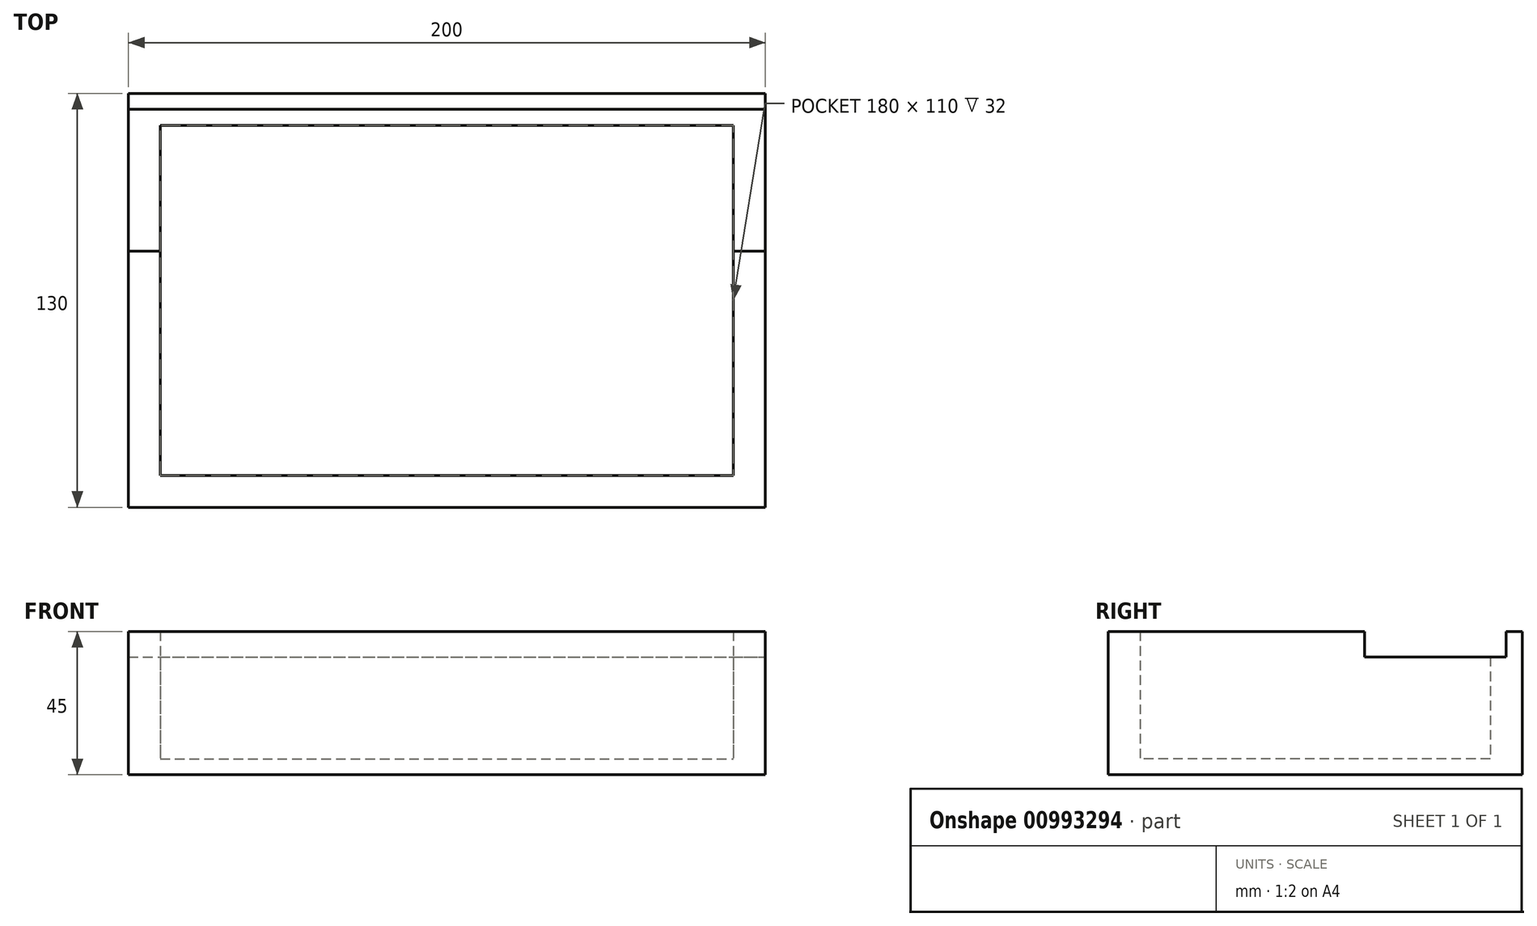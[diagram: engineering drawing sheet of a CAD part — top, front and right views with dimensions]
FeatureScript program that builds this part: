
annotation { "Feature Type Name" : "Feature", "Feature Type Description" : "" }
export const myFeature = defineFeature(function(context is Context, id is Id, definition is map)
    precondition{}
    {
        {
            var Q0;
            Q0=qCreatedBy(makeId("Top.planeOp"),FACE);
            var sketch = newSketch(context, id + "F0", { "sketchPlane" : qUnion([Q0])});
            skLineSegment(sketch, "E0.bottom", {"start": v(100, 65) * mm, "end": v(-100, 65) * mm});
            skLineSegment(sketch, "E0.top", {"start": v(100, -65) * mm, "end": v(-100, -65) * mm});
            skLineSegment(sketch, "E0.left", {"start": v(100, 65) * mm, "end": v(100, -65) * mm});
            skLineSegment(sketch, "E0.right", {"start": v(-100, 65) * mm, "end": v(-100, -65) * mm});
            skPoint(sketch, "E0.middle", {"position": v(0, 0) * mm});
            skSolve(sketch);
        }
        {
            var Q0;
            Q0 = qSketchRegion(id + "F0", true);
            extrude(context, id + "F1", {"entities" : qUnion([Q0]), "depth" : 5 * mm, "offsetDistance" : 25 * mm});
        }
        {
            var Q0;
            Q0=makeQuery(id+"F1.opExtrude","CAP_FACE",FACE,{"disambiguationData":[OSD([sQuery(id+"F0.wireOp",EDGE,"E0.bottom"),sQuery(id+"F0.wireOp",EDGE,"E0.top"),sQuery(id+"F0.wireOp",EDGE,"E0.left"),sQuery(id+"F0.wireOp",EDGE,"E0.right")])],"isStart":false});
            var sketch = newSketch(context, id + "F2", { "sketchPlane" : qUnion([Q0])});
            skLineSegment(sketch, "E1.bottom", {"start": v(-100, 65) * mm, "end": v(100, 65) * mm});
            skLineSegment(sketch, "E1.top", {"start": v(-100, 55) * mm, "end": v(100, 55) * mm});
            skLineSegment(sketch, "E1.left", {"start": v(-100, 65) * mm, "end": v(-100, 55) * mm});
            skLineSegment(sketch, "E1.right", {"start": v(100, 65) * mm, "end": v(100, 55) * mm});
            skSolve(sketch);
        }
        {
            var Q0;
            Q0 = qSketchRegion(id + "F2", true);
            extrude(context, id + "F3", {"entities" : qUnion([Q0]), "operationType" : NewBodyOperationType.ADD, "depth" : 32 * mm, "offsetDistance" : 25 * mm});
        }
        {
            var Q0;
            Q0=makeQuery(id+"F3.opExtrude","CAP_FACE",FACE,{"disambiguationData":[OSD([sQuery(id+"F2.wireOp",EDGE,"E1.bottom"),sQuery(id+"F2.wireOp",EDGE,"E1.top"),sQuery(id+"F2.wireOp",EDGE,"E1.left"),sQuery(id+"F2.wireOp",EDGE,"E1.right")])],"isStart":false});
            var sketch = newSketch(context, id + "F4", { "sketchPlane" : qUnion([Q0])});
            skLineSegment(sketch, "E2.bottom", {"start": v(-100, 65) * mm, "end": v(100, 65) * mm});
            skLineSegment(sketch, "E2.top", {"start": v(-100, 60) * mm, "end": v(100, 60) * mm});
            skLineSegment(sketch, "E2.left", {"start": v(-100, 65) * mm, "end": v(-100, 60) * mm});
            skLineSegment(sketch, "E2.right", {"start": v(100, 65) * mm, "end": v(100, 60) * mm});
            skSolve(sketch);
        }
        {
            var Q0;
            Q0 = qSketchRegion(id + "F4", true);
            extrude(context, id + "F5", {"entities" : qUnion([Q0]), "operationType" : NewBodyOperationType.ADD, "depth" : 8 * mm, "offsetDistance" : 25 * mm});
        }
        {
            var Q0;
            Q0=makeQuery(id+"F1.opExtrude","CAP_FACE",FACE,{"disambiguationData":[OSD([sQuery(id+"F0.wireOp",EDGE,"E0.bottom"),sQuery(id+"F0.wireOp",EDGE,"E0.top"),sQuery(id+"F0.wireOp",EDGE,"E0.left"),sQuery(id+"F0.wireOp",EDGE,"E0.right")])],"isStart":false});
            var sketch = newSketch(context, id + "F6", { "sketchPlane" : qUnion([Q0])});
            skLineSegment(sketch, "E3.bottom", {"start": v(-100, 55) * mm, "end": v(-90, 55) * mm});
            skLineSegment(sketch, "E3.top", {"start": v(-100, -65) * mm, "end": v(-90, -65) * mm});
            skLineSegment(sketch, "E3.left", {"start": v(-100, 55) * mm, "end": v(-100, -65) * mm});
            skLineSegment(sketch, "E3.right", {"start": v(-90, 55) * mm, "end": v(-90, -65) * mm});
            skSolve(sketch);
        }
        {
            var Q0;
            Q0 = qSketchRegion(id + "F6", true);
            extrude(context, id + "F7", {"entities" : qUnion([Q0]), "operationType" : NewBodyOperationType.ADD, "depth" : 32 * mm, "offsetDistance" : 25 * mm});
        }
        {
            var Q0;
            Q0=makeQuery(id+"F1.opExtrude","CAP_FACE",FACE,{"disambiguationData":[OSD([sQuery(id+"F0.wireOp",EDGE,"E0.bottom"),sQuery(id+"F0.wireOp",EDGE,"E0.top"),sQuery(id+"F0.wireOp",EDGE,"E0.left"),sQuery(id+"F0.wireOp",EDGE,"E0.right")])],"isStart":false});
            var sketch = newSketch(context, id + "F8", { "sketchPlane" : qUnion([Q0])});
            skLineSegment(sketch, "E4.bottom", {"start": v(100, 55) * mm, "end": v(90, 55) * mm});
            skLineSegment(sketch, "E4.top", {"start": v(100, -65) * mm, "end": v(90, -65) * mm});
            skLineSegment(sketch, "E4.left", {"start": v(100, 55) * mm, "end": v(100, -65) * mm});
            skLineSegment(sketch, "E4.right", {"start": v(90, 55) * mm, "end": v(90, -65) * mm});
            skSolve(sketch);
        }
        {
            var Q0;
            Q0 = qSketchRegion(id + "F8", true);
            extrude(context, id + "F9", {"entities" : qUnion([Q0]), "operationType" : NewBodyOperationType.ADD, "depth" : 32 * mm, "offsetDistance" : 25 * mm});
        }
        {
            var Q0;
            Q0=makeQuery(id+"F1.opExtrude","CAP_FACE",FACE,{"disambiguationData":[OSD([sQuery(id+"F0.wireOp",EDGE,"E0.bottom"),sQuery(id+"F0.wireOp",EDGE,"E0.top"),sQuery(id+"F0.wireOp",EDGE,"E0.left"),sQuery(id+"F0.wireOp",EDGE,"E0.right")])],"isStart":false});
            var sketch = newSketch(context, id + "F10", { "sketchPlane" : qUnion([Q0])});
            skLineSegment(sketch, "E5.bottom", {"start": v(-90, -65) * mm, "end": v(90, -65) * mm});
            skLineSegment(sketch, "E5.top", {"start": v(-90, -55) * mm, "end": v(90, -55) * mm});
            skLineSegment(sketch, "E5.left", {"start": v(-90, -65) * mm, "end": v(-90, -55) * mm});
            skLineSegment(sketch, "E5.right", {"start": v(90, -65) * mm, "end": v(90, -55) * mm});
            skSolve(sketch);
        }
        {
            var Q0;
            Q0 = qSketchRegion(id + "F10", true);
            extrude(context, id + "F11", {"entities" : qUnion([Q0]), "operationType" : NewBodyOperationType.ADD, "depth" : 40 * mm, "offsetDistance" : 25 * mm});
        }
        {
            var Q0;
            Q0=makeQuery(id+"F9.boolean.opBoolean","MERGE",FACE,{"derivedFrom":[makeQuery(id+"F7.boolean.opBoolean","MERGE",FACE,{"derivedFrom":[makeQuery(id+"F3.opExtrude","CAP_FACE",FACE,{"disambiguationData":[OSD([sQuery(id+"F2.wireOp",EDGE,"E1.bottom"),sQuery(id+"F2.wireOp",EDGE,"E1.top"),sQuery(id+"F2.wireOp",EDGE,"E1.left"),sQuery(id+"F2.wireOp",EDGE,"E1.right")])],"isStart":false}),makeQuery(id+"F7.opExtrude","CAP_FACE",FACE,{"disambiguationData":[OSD([sQuery(id+"F6.wireOp",EDGE,"E3.bottom"),sQuery(id+"F6.wireOp",EDGE,"E3.top"),sQuery(id+"F6.wireOp",EDGE,"E3.left"),sQuery(id+"F6.wireOp",EDGE,"E3.right")])],"isStart":false})]}),makeQuery(id+"F9.opExtrude","CAP_FACE",FACE,{"disambiguationData":[OSD([sQuery(id+"F8.wireOp",EDGE,"E4.bottom"),sQuery(id+"F8.wireOp",EDGE,"E4.top"),sQuery(id+"F8.wireOp",EDGE,"E4.left"),sQuery(id+"F8.wireOp",EDGE,"E4.right")])],"isStart":false})]});
            var sketch = newSketch(context, id + "F12", { "sketchPlane" : qUnion([Q0])});
            skLineSegment(sketch, "E6.bottom", {"start": v(90, -65) * mm, "end": v(100, -65) * mm});
            skLineSegment(sketch, "E6.top", {"start": v(90, 15.5) * mm, "end": v(100, 15.5) * mm});
            skLineSegment(sketch, "E6.left", {"start": v(90, -65) * mm, "end": v(90, 15.5) * mm});
            skLineSegment(sketch, "E6.right", {"start": v(100, -65) * mm, "end": v(100, 15.5) * mm});
            skSolve(sketch);
        }
        {
            var Q0;
            Q0 = qSketchRegion(id + "F12", true);
            extrude(context, id + "F13", {"entities" : qUnion([Q0]), "operationType" : NewBodyOperationType.ADD, "depth" : 8 * mm, "offsetDistance" : 25 * mm});
        }
        {
            var Q0;
            Q0=makeQuery(id+"F9.boolean.opBoolean","MERGE",FACE,{"derivedFrom":[makeQuery(id+"F7.boolean.opBoolean","MERGE",FACE,{"derivedFrom":[makeQuery(id+"F3.opExtrude","CAP_FACE",FACE,{"disambiguationData":[OSD([sQuery(id+"F2.wireOp",EDGE,"E1.bottom"),sQuery(id+"F2.wireOp",EDGE,"E1.top"),sQuery(id+"F2.wireOp",EDGE,"E1.left"),sQuery(id+"F2.wireOp",EDGE,"E1.right")])],"isStart":false}),makeQuery(id+"F7.opExtrude","CAP_FACE",FACE,{"disambiguationData":[OSD([sQuery(id+"F6.wireOp",EDGE,"E3.bottom"),sQuery(id+"F6.wireOp",EDGE,"E3.top"),sQuery(id+"F6.wireOp",EDGE,"E3.left"),sQuery(id+"F6.wireOp",EDGE,"E3.right")])],"isStart":false})]}),makeQuery(id+"F9.opExtrude","CAP_FACE",FACE,{"disambiguationData":[OSD([sQuery(id+"F8.wireOp",EDGE,"E4.bottom"),sQuery(id+"F8.wireOp",EDGE,"E4.top"),sQuery(id+"F8.wireOp",EDGE,"E4.left"),sQuery(id+"F8.wireOp",EDGE,"E4.right")])],"isStart":false})]});
            var sketch = newSketch(context, id + "F14", { "sketchPlane" : qUnion([Q0])});
            skLineSegment(sketch, "E7.bottom", {"start": v(-100, -65) * mm, "end": v(-90, -65) * mm});
            skLineSegment(sketch, "E7.top", {"start": v(-100, 15.5) * mm, "end": v(-90, 15.5) * mm});
            skLineSegment(sketch, "E7.left", {"start": v(-100, -65) * mm, "end": v(-100, 15.5) * mm});
            skLineSegment(sketch, "E7.right", {"start": v(-90, -65) * mm, "end": v(-90, 15.5) * mm});
            skSolve(sketch);
        }
        {
            var Q0;
            Q0 = qSketchRegion(id + "F14", true);
            extrude(context, id + "F15", {"entities" : qUnion([Q0]), "operationType" : NewBodyOperationType.ADD, "depth" : 8 * mm, "offsetDistance" : 25 * mm});
        }
    });
